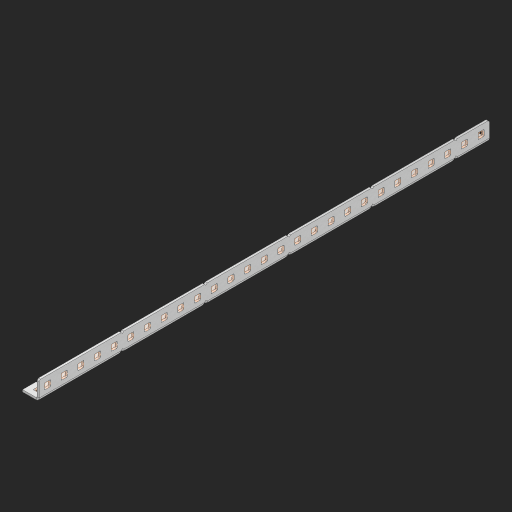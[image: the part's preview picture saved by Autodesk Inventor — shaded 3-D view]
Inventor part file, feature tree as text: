
AUTODESK INVENTOR PART (.ipt)
format: ipt  version: 2023 (Build 270158000, 158)  size: 1,173,504 bytes
history: native  units: in
note: dims shown in document units (in); Inventor stores cm internally (conversion verified against a paired STEP export)
features: other x229, extrude x79, sheet_metal_op x11, sketch x10, pattern_linear x2, mirror x1, chamfer x1
ambient origin geometry x8: Origin, YZ Plane, XZ Plane, XY Plane, X Axis, Y Axis, Z Axis, Center Point
bodies: Solid1 (feature_tree), Body (feature_tree)
feature tree (333):
  other  "Alu Half C 1x2x1x27"
  other  "Table"
  other  "Alu C 1x2x1x35"
  other  "Alu C 1x2x1x34"
  other  "Alu C 1x2x1x33"
  other  "Alu C 1x2x1x32"
  other  "Alu C 1x2x1x31"
  other  "Alu C 1x2x1x30"
  other  "Alu C 1x2x1x29"
  other  "Alu C 1x2x1x28"
  other  "Alu C 1x2x1x27"
  other  "Alu C 1x2x1x26"
  other  "Alu C 1x2x1x25"
  other  "Alu C 1x2x1x24"
  other  "Alu C 1x2x1x23"
  other  "Alu C 1x2x1x22"
  other  "Alu C 1x2x1x21"
  other  "Alu C 1x2x1x20"
  other  "Alu C 1x2x1x19"
  other  "Alu C 1x2x1x18"
  other  "Alu C 1x2x1x17"
  other  "Alu C 1x2x1x16"
  other  "Alu C 1x2x1x15"
  other  "Alu C 1x2x1x14"
  other  "Alu C 1x2x1x13"
  other  "Alu C 1x2x1x12"
  other  "Alu C 1x2x1x11"
  other  "Alu C 1x2x1x10"
  other  "Alu C 1x2x1x9"
  other  "Alu C 1x2x1x8"
  other  "Alu C 1x2x1x7"
  other  "Alu C 1x2x1x6"
  other  "Alu C 1x2x1x5"
  other  "Alu C 1x2x1x4"
  other  "Alu C 1x2x1x3"
  other  "Alu C 1x2x1x2"
  other  "Alu C 1x2x1x1"
  other  "Steel C 1x2x1x35"
  other  "Steel C 1x2x1x34"
  other  "Steel C 1x2x1x33"
  other  "Steel C 1x2x1x32"
  other  "Steel C 1x2x1x31"
  other  "Steel C 1x2x1x30"
  other  "Steel C 1x2x1x29"
  other  "Steel C 1x2x1x28"
  other  "Steel C 1x2x1x27"
  other  "Steel C 1x2x1x26"
  other  "Steel C 1x2x1x25"
  other  "Steel C 1x2x1x24"
  other  "Steel C 1x2x1x23"
  other  "Steel C 1x2x1x22"
  other  "Steel C 1x2x1x21"
  other  "Steel C 1x2x1x20"
  other  "Steel C 1x2x1x19"
  other  "Steel C 1x2x1x18"
  other  "Steel C 1x2x1x17"
  other  "Steel C 1x2x1x16"
  other  "Steel C 1x2x1x15"
  other  "Steel C 1x2x1x14"
  other  "Steel C 1x2x1x13"
  other  "Steel C 1x2x1x12"
  other  "Steel C 1x2x1x11"
  other  "Steel C 1x2x1x10"
  other  "Steel C 1x2x1x9"
  other  "Steel C 1x2x1x8"
  other  "Steel C 1x2x1x7"
  other  "Steel C 1x2x1x6"
  other  "Steel C 1x2x1x5"
  other  "Steel C 1x2x1x4"
  other  "Steel C 1x2x1x3"
  other  "Steel C 1x2x1x2"
  other  "Steel C 1x2x1x1"
  other  "Alu Half C 1x2x1x35"
  other  "Alu Half C 1x2x1x34"
  other  "Alu Half C 1x2x1x33"
  other  "Alu Half C 1x2x1x32"
  other  "Alu Half C 1x2x1x31"
  other  "Alu Half C 1x2x1x30"
  other  "Alu Half C 1x2x1x29"
  other  "Alu Half C 1x2x1x28"
  other  "Alu Half C 1x2x1x26"
  other  "Alu Half C 1x2x1x25"
  other  "Alu Half C 1x2x1x24"
  other  "Alu Half C 1x2x1x23"
  other  "Alu Half C 1x2x1x22"
  other  "Alu Half C 1x2x1x21"
  other  "Alu Half C 1x2x1x20"
  other  "Alu Half C 1x2x1x19"
  other  "Alu Half C 1x2x1x18"
  other  "Alu Half C 1x2x1x17"
  other  "Alu Half C 1x2x1x16"
  other  "Alu Half C 1x2x1x15"
  other  "Alu Half C 1x2x1x14"
  other  "Alu Half C 1x2x1x13"
  other  "Alu Half C 1x2x1x12"
  other  "Alu Half C 1x2x1x11"
  other  "Alu Half C 1x2x1x10"
  other  "Alu Half C 1x2x1x9"
  other  "Alu Half C 1x2x1x8"
  other  "Alu Half C 1x2x1x7"
  other  "Alu Half C 1x2x1x6"
  other  "Alu Half C 1x2x1x5"
  other  "Alu Half C 1x2x1x4"
  other  "Alu Half C 1x2x1x3"
  other  "Alu Half C 1x2x1x2"
  other  "Alu Half C 1x2x1x1"
  other  "Steel Half C 1x2x1x35"
  other  "Steel Half C 1x2x1x34"
  other  "Steel Half C 1x2x1x33"
  other  "Steel Half C 1x2x1x32"
  other  "Steel Half C 1x2x1x31"
  other  "Steel Half C 1x2x1x30"
  other  "Steel Half C 1x2x1x29"
  other  "Steel Half C 1x2x1x28"
  other  "Steel Half C 1x2x1x27"
  other  "Steel Half C 1x2x1x26"
  other  "Steel Half C 1x2x1x25"
  other  "Steel Half C 1x2x1x24"
  other  "Steel Half C 1x2x1x23"
  other  "Steel Half C 1x2x1x22"
  other  "Steel Half C 1x2x1x21"
  other  "Steel Half C 1x2x1x20"
  other  "Steel Half C 1x2x1x19"
  other  "Steel Half C 1x2x1x18"
  other  "Steel Half C 1x2x1x17"
  other  "Steel Half C 1x2x1x16"
  other  "Steel Half C 1x2x1x15"
  other  "Steel Half C 1x2x1x14"
  other  "Steel Half C 1x2x1x13"
  other  "Steel Half C 1x2x1x12"
  other  "Steel Half C 1x2x1x11"
  other  "Steel Half C 1x2x1x10"
  other  "Steel Half C 1x2x1x9"
  other  "Steel Half C 1x2x1x8"
  other  "Steel Half C 1x2x1x7"
  other  "Steel Half C 1x2x1x6"
  other  "Steel Half C 1x2x1x5"
  other  "Steel Half C 1x2x1x4"
  other  "Steel Half C 1x2x1x3"
  other  "Steel Half C 1x2x1x2"
  other  "Steel Half C 1x2x1x1"
  sheet_metal_op  "Flanges"
  other  "Flange Pattern Plane"
  other  "Flange Pattern Sketch"
  sheet_metal_op  "Flange Pattern"
  sheet_metal_op  "Body Pattern"
  pattern_linear  "Center Pattern"  Spacing1=0.0625in  [1 undecoded]
  other  "Arc Length"
  mirror  "Notch Mirror"
  pattern_linear  "Notch Pattern"  Spacing1=0.182in  [1 undecoded]
  chamfer  "End Chamfer"
  extrude  "Half Cut"  Depth=0.02in
  sketch  "Sketch1"  dims[d0=1.0in]
  other  "Plate1"
  sketch  "Sketch2"  dims[d1=13.5in]
  other  "Plate2"
  sheet_metal_op  "Bend1"
  sheet_metal_op  "Corner1"
  sketch  "Sketch3"  dims[d2=0.0625in]
  sketch  "Sketch7"  dims[d3=0.0625in]
  other  "Srf1"
  other  "Srf2"
  sketch  "Sketch8"  dims[d4=0.0312in]
  sketch  "Sketch9"  dims[d5=0.125in]
  other  "Srf91"
  sheet_metal_op  "Body Pattern Sketch"
  other  "Srf92"
  sketch  "Sketch13"  dims[d6=0.0625in]
  sketch  "Sketch14"  dims[d7=0.5in d8=90.0deg d9=0.0312in]
  sketch  "Sketch15"  dims[d10=0.25in]
  sketch  "Sketch16"  dims[d11=0.0625in d12=0.0625in d16=0.182in d17=0.02in d18=0.0625in d19=0.0in d20=0.25in d21=0.25in d38=10.6299in d40=0.5in d41=0.3937in d43=1.0in d46=0.172in d47=1.0in d48=0.0in d49=0.182in d50=0.02in d51=0.25in d52=0.25in d53=0.0625in d54=0.0in d55=0.172in d56=1.0in d57=0.0in d58=0.25in d60=10.6299in d62=0.5in d63=0.3937in d65=0.5in d85=0.1473in d86=0.1782in d88=0.04in d89=0.0625in d90=0.0in d91=0.04in d92=0.0491in d95=2.5in d96=0.04in d97=0.25in d98=45.0deg d99=0.25in d100=0.5in d101=0.0in d102=2.497in d106=0.182in d107=0.02in d108=0.5in d109=0.5in d110=0.0625in d111=0.0in d112=0.172in d113=0.5in d114=0.0in d117=0.5in d118=0.5in d119=0.5in]
  other  "Srf786"
  other  "Srf823"
  other  "Srf824"
  other  "Srf825"
  other  "Srf826"
  other  "Srf827"
  other  "Srf828"
  other  "Srf829"
  other  "Srf856"
  other  "Srf857"
  other  "Srf858"
  other  "Srf859"
  other  "Srf860"
  other  "Srf861"
  other  "Srf862"
  other  "Srf889"
  other  "Srf890"
  other  "Srf891"
  other  "Srf892"
  other  "Srf893"
  other  "Srf894"
  other  "Srf895"
  other  "Srf896"
  other  "Srf922"
  other  "Srf923"
  other  "Srf924"
  other  "Srf925"
  other  "Srf926"
  other  "Srf959"
  other  "Srf960"
  other  "Srf961"
  other  "Srf962"
  other  "Srf963"
  other  "Srf996"
  other  "Srf997"
  other  "Srf998"
  other  "Srf999"
  other  "Srf1000"
  other  "Srf1143"
  other  "Srf1144"
  other  "Srf1145"
  other  "Srf1146"
  other  "Srf1147"
  other  "Srf1148"
  other  "Srf1149"
  other  "Srf1150"
  other  "Srf1151"
  other  "Srf1152"
  other  "Srf1153"
  other  "Srf1154"
  other  "Srf1155"
  other  "Srf1199"
  other  "Srf1200"
  other  "Srf1201"
  other  "Srf1202"
  other  "Srf1203"
  other  "Srf1204"
  other  "Srf1205"
  other  "Srf1206"
  other  "Srf1207"
  other  "Srf1208"
  other  "Srf1209"
  other  "Srf1210"
  other  "Srf1211"
  other  "Srf1255"
  other  "Srf1256"
  other  "Srf1257"
  other  "Srf1258"
  other  "Srf1259"
  other  "Srf1260"
  other  "Srf1261"
  other  "Srf1262"
  other  "Srf1263"
  other  "Srf1264"
  other  "Srf1265"
  other  "Srf1266"
  other  "Srf1267"
  sheet_metal_op  "Flange Stamp"
  sheet_metal_op  "Flange Circle"
  sheet_metal_op  "Body Stamp"
  sheet_metal_op  "Body Circle"
  other  "Center Stamp"
  other  "Center Circle"
  sheet_metal_op  "Notch"
  extrude  "ExtrusionSrf2"  Depth=0.0625in
  extrude  "ExtrusionSrf92"  TaperAngle=0.0deg  [1 undecoded]
  extrude  "ExtrusionSrf823"  Depth=0.5in
  extrude  "ExtrusionSrf824"  Depth=0.5in
  extrude  "ExtrusionSrf825"  Depth=0.5in
  extrude  "ExtrusionSrf826"  Depth=0.5in
  extrude  "ExtrusionSrf827"  Depth=1.0in TaperAngle=0.0deg
  extrude  "ExtrusionSrf828"  Depth=0.182in
  extrude  "ExtrusionSrf829"  Depth=0.02in
  extrude  "ExtrusionSrf856"  Depth=0.5in
  extrude  "ExtrusionSrf857"  Depth=0.5in
  extrude  "ExtrusionSrf858"  Depth=0.0625in
  extrude  "ExtrusionSrf859"  TaperAngle=0.0deg  [1 undecoded]
  extrude  "ExtrusionSrf860"  Depth=0.5in
  extrude  "ExtrusionSrf861"  Depth=1.0in TaperAngle=0.0deg
  extrude  "ExtrusionSrf862"  Depth=0.5in
  extrude  "ExtrusionSrf889"  Depth=0.5in
  extrude  "ExtrusionSrf890"  Depth=0.5in
  extrude  "ExtrusionSrf891"  Depth=0.5in
  extrude  "ExtrusionSrf892"  Depth=0.5in
  extrude  "ExtrusionSrf893"  Depth=0.5in
  extrude  "ExtrusionSrf894"  Depth=0.0625in
  extrude  "ExtrusionSrf895"  TaperAngle=0.0deg  [1 undecoded]
  extrude  "ExtrusionSrf896"  Depth=0.5in
  extrude  "ExtrusionSrf922"  Depth=0.5in
  extrude  "ExtrusionSrf923"  Depth=0.5in
  extrude  "ExtrusionSrf924"  Depth=0.5in TaperAngle=45.0deg
  extrude  "ExtrusionSrf925"  Depth=0.5in
  extrude  "ExtrusionSrf926"  Depth=0.5in TaperAngle=0.0deg
  extrude  "ExtrusionSrf959"  Depth=0.5in
  extrude  "ExtrusionSrf960"  Depth=0.182in
  extrude  "ExtrusionSrf961"  Depth=0.02in
  extrude  "ExtrusionSrf962"  Depth=0.5in
  extrude  "ExtrusionSrf963"  Depth=0.5in
  extrude  "ExtrusionSrf996"  Depth=0.0625in
  extrude  "ExtrusionSrf997"  TaperAngle=0.0deg  [1 undecoded]
  extrude  "ExtrusionSrf998"  Depth=0.5in
  extrude  "ExtrusionSrf999"  Depth=0.5in TaperAngle=0.0deg
  extrude  "ExtrusionSrf1000"  Depth=0.5in
  extrude  "ExtrusionSrf1143"  Depth=0.5in
  extrude  "ExtrusionSrf1144"  Depth=0.5in
  extrude  "ExtrusionSrf1145"  [1 undecoded]
  extrude  "ExtrusionSrf1146"  [1 undecoded]
  extrude  "ExtrusionSrf1147"  [1 undecoded]
  extrude  "ExtrusionSrf1148"  [1 undecoded]
  extrude  "ExtrusionSrf1149"  [1 undecoded]
  extrude  "ExtrusionSrf1150"  [1 undecoded]
  extrude  "ExtrusionSrf1151"  [1 undecoded]
  extrude  "ExtrusionSrf1152"  [1 undecoded]
  extrude  "ExtrusionSrf1153"  [1 undecoded]
  extrude  "ExtrusionSrf1154"  [1 undecoded]
  extrude  "ExtrusionSrf1155"  [1 undecoded]
  extrude  "ExtrusionSrf1199"  [1 undecoded]
  extrude  "ExtrusionSrf1200"  [1 undecoded]
  extrude  "ExtrusionSrf1201"  [1 undecoded]
  extrude  "ExtrusionSrf1202"  [1 undecoded]
  extrude  "ExtrusionSrf1203"  [1 undecoded]
  extrude  "ExtrusionSrf1204"  [1 undecoded]
  extrude  "ExtrusionSrf1205"  [1 undecoded]
  extrude  "ExtrusionSrf1206"  [1 undecoded]
  extrude  "ExtrusionSrf1207"  [1 undecoded]
  extrude  "ExtrusionSrf1208"  [1 undecoded]
  extrude  "ExtrusionSrf1209"  [1 undecoded]
  extrude  "ExtrusionSrf1210"  [1 undecoded]
  extrude  "ExtrusionSrf1211"  [1 undecoded]
  extrude  "ExtrusionSrf1255"  [1 undecoded]
  extrude  "ExtrusionSrf1256"  [1 undecoded]
  extrude  "ExtrusionSrf1257"  [1 undecoded]
  extrude  "ExtrusionSrf1258"  [1 undecoded]
  extrude  "ExtrusionSrf1259"  [1 undecoded]
  extrude  "ExtrusionSrf1260"  [1 undecoded]
  extrude  "ExtrusionSrf1261"  [1 undecoded]
  extrude  "ExtrusionSrf1262"  [1 undecoded]
  extrude  "ExtrusionSrf1263"  [1 undecoded]
  extrude  "ExtrusionSrf1264"  [1 undecoded]
  extrude  "ExtrusionSrf1265"  [1 undecoded]
  extrude  "ExtrusionSrf1266"  [1 undecoded]
  extrude  "ExtrusionSrf1267"  [1 undecoded]
note: 43 required parameter values undecoded (feature->parameter linkage not recoverable at this tier; creation-order binding heuristic only, values carry confidence <= 0.55)
